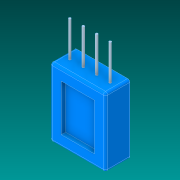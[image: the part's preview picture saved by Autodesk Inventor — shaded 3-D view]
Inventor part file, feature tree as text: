
AUTODESK INVENTOR PART (.ipt)
format: ipt  version: 2019 (Build 230136000, 136)  size: 135,680 bytes
history: native  units: mm
features: extrude x3, sketch x3, fillet x1
ambient origin geometry x8: Origin, YZ Plane, XZ Plane, XY Plane, X Axis, Y Axis, Z Axis, Center Point
bodies: Solid1 (feature_tree)
feature tree (7):
  extrude  "Extrusion1"  Depth=15.5mm
  extrude  "Extrusion2"  Depth=0.5mm
  fillet  "Fillet1"  Radius=0.5mm
  extrude  "Extrusion3"  Depth=0.5mm
  sketch  "Sketch1"  dims[d0=12.5mm d1=15.5mm]
  sketch  "Sketch2"  dims[d2=5.5mm d3=0.0mm d27=0.5mm d28=0.5mm]
  sketch  "Sketch3"  dims[d29=0.5mm d30=0.5mm d31=8.0mm d32=0.0mm d33=0.5mm d35=1.0mm d36=0.0mm]
